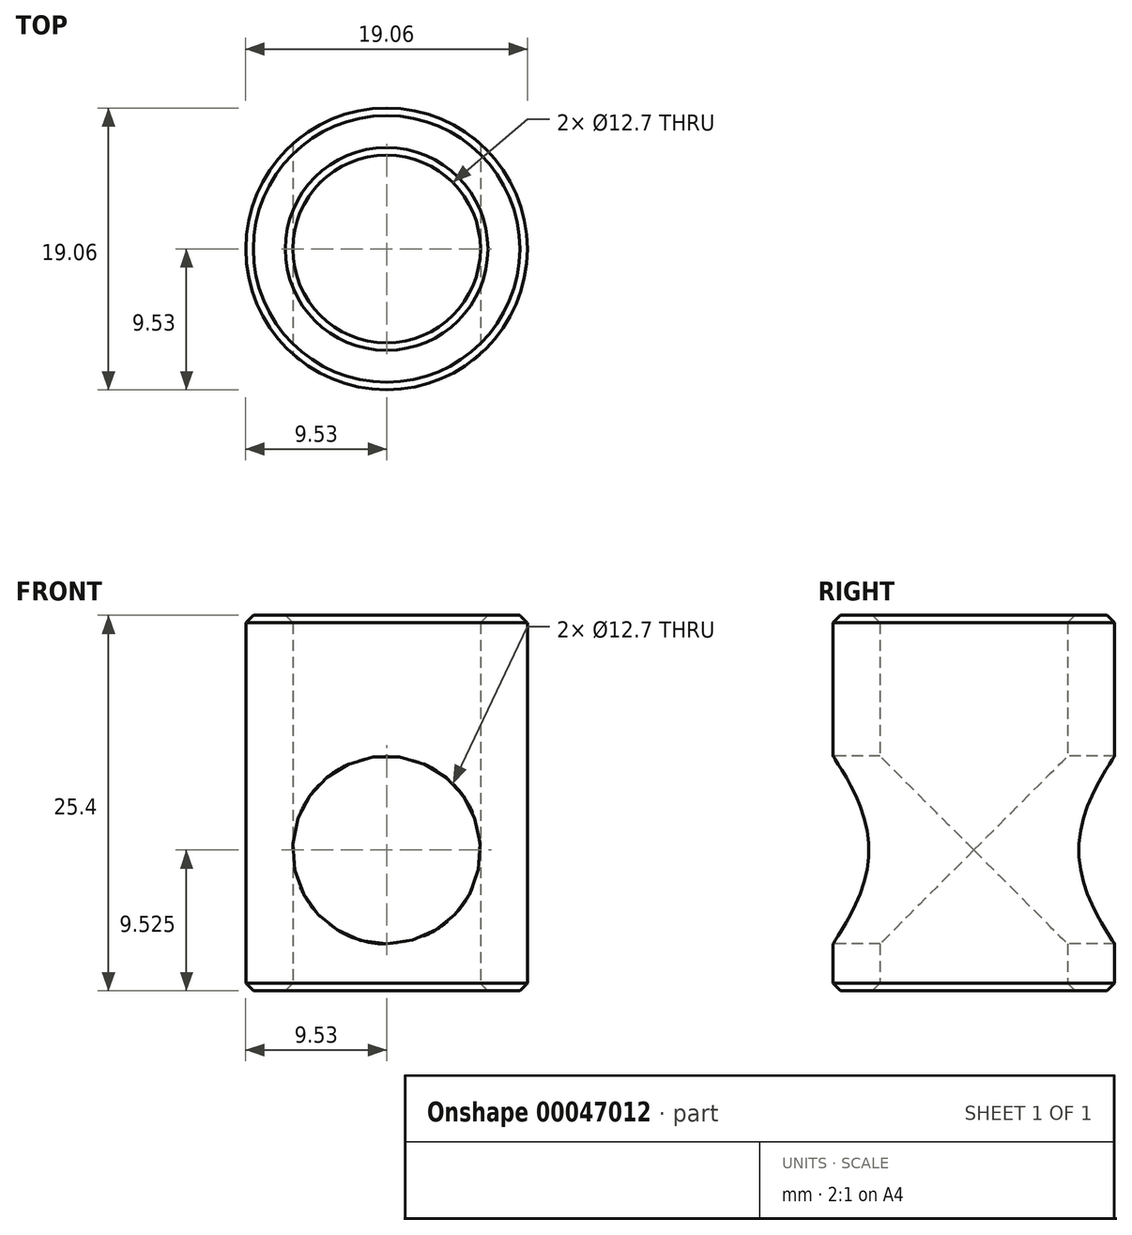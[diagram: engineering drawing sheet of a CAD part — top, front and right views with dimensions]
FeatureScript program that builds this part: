
annotation { "Feature Type Name" : "Feature", "Feature Type Description" : "" }
export const myFeature = defineFeature(function(context is Context, id is Id, definition is map)
    precondition{}
    {
        {
            var Q0;
            Q0=qCreatedBy(makeId("Top.planeOp"),FACE);
            var sketch = newSketch(context, id + "F0", { "sketchPlane" : qUnion([Q0])});
            skCircle(sketch, "E0", {"center": v(0, 0) * mm, "radius": 9.53 * mm});
            skCircle(sketch, "E1", {"center": v(0, 0) * mm, "radius": 6.35 * mm});
            skSolve(sketch);
        }
        {
            var Q0;
            Q0=makeQuery(id+"F0.imprint","IMPRINT",FACE,{"disambiguationData":[TD([[makeQuery(id+"F0.imprint","IMPRINT",EDGE,{"derivedFrom":sQuery(id+"F0.wireOp",EDGE,"E0")}),1.0]])]});
            extrude(context, id + "F1", {"entities" : qUnion([Q0]), "depth" : 25.4 * mm});
        }
        {
            var Q0;
            Q0=qCreatedBy(makeId("Front.planeOp"),FACE);
            var sketch = newSketch(context, id + "F2", { "sketchPlane" : qUnion([Q0])});
            skLineSegment(sketch, "E2", {"start": v(-6.35, 0) * mm, "end": v(-6.35, 25.4) * mm});
            skLineSegment(sketch, "E3", {"start": v(6.35, 25.4) * mm, "end": v(6.35, 0) * mm});
            skLineSegment(sketch, "E4", {"start": v(-9.53, 0) * mm, "end": v(-9.53, 25.4) * mm});
            skLineSegment(sketch, "E5", {"start": v(9.53, 25.4) * mm, "end": v(9.53, 0) * mm});
            skCircle(sketch, "E6", {"center": v(0, 9.53) * mm, "radius": 6.35 * mm});
            skSolve(sketch);
        }
        {
            var Q0;
            Q0=makeQuery(id+"F2.imprint","IMPRINT",FACE,{"disambiguationData":[TD([[makeQuery(id+"F2.imprint","IMPRINT",EDGE,{"derivedFrom":sQuery(id+"F2.wireOp",EDGE,"E6")}),1.0]])]});
            extrude(context, id + "F3", {"entities" : qUnion([Q0]), "operationType" : NewBodyOperationType.REMOVE, "endBound" : BoundingType.SYMMETRIC, "oppositeDirection" : true, "depth" : 25.4 * mm});
        }
        {
            var Q0;
            Q0=makeQuery(id+"F1.opExtrude","CAP_EDGE",EDGE,{"disambiguationData":[OSD([sQuery(id+"F0.wireOp",EDGE,"E1")])],"isStart":false});
            var Q1;
            Q1=makeQuery(id+"F1.opExtrude","CAP_EDGE",EDGE,{"disambiguationData":[OSD([sQuery(id+"F0.wireOp",EDGE,"E0")])],"isStart":false});
            var Q2;
            Q2=makeQuery(id+"F1.opExtrude","CAP_EDGE",EDGE,{"disambiguationData":[OSD([sQuery(id+"F0.wireOp",EDGE,"E1")])],"isStart":true});
            var Q3;
            Q3=makeQuery(id+"F1.opExtrude","CAP_EDGE",EDGE,{"disambiguationData":[OSD([sQuery(id+"F0.wireOp",EDGE,"E0")])],"isStart":true});
            chamfer(context, id + "F4", {"entities" : qUnion([Q0, Q1, Q2, Q3]), "width" : 0.5 * mm, "tangentPropagation" : true});
        }
    });
